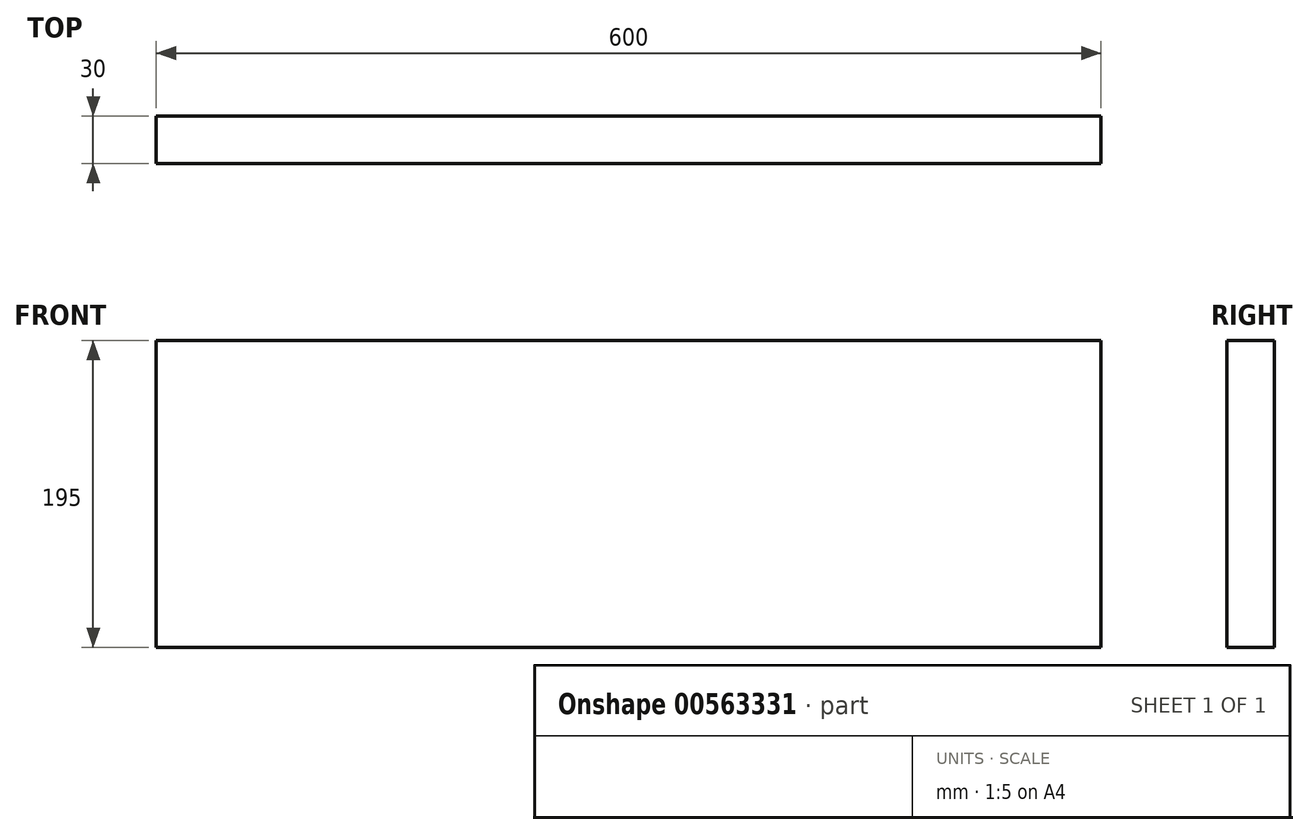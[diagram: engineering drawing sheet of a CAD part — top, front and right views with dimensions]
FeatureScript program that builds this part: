
annotation { "Feature Type Name" : "Feature", "Feature Type Description" : "" }
export const myFeature = defineFeature(function(context is Context, id is Id, definition is map)
    precondition{}
    {
        {
            var Q0;
            Q0=qCreatedBy(makeId("Top.planeOp"),FACE);
            var sketch = newSketch(context, id + "F0", { "sketchPlane" : qUnion([Q0])});
            skLineSegment(sketch, "E0.bottom", {"start": v(0, 0) * mm, "end": v(600, 0) * mm});
            skLineSegment(sketch, "E0.top", {"start": v(0, 30) * mm, "end": v(600, 30) * mm});
            skLineSegment(sketch, "E0.left", {"start": v(0, 0) * mm, "end": v(0, 30) * mm});
            skLineSegment(sketch, "E0.right", {"start": v(600, 0) * mm, "end": v(600, 30) * mm});
            skSolve(sketch);
        }
        {
            var Q0;
            Q0=makeQuery(id+"F0.imprint","IMPRINT",FACE,{"disambiguationData":[TD([[makeQuery(id+"F0.imprint","IMPRINT",EDGE,{"derivedFrom":sQuery(id+"F0.wireOp",EDGE,"E0.bottom")}),1.0]])]});
            extrude(context, id + "F1", {"entities" : qUnion([Q0]), "depth" : 195 * mm, "offsetDistance" : 25 * mm});
        }
    });
